# Revit family: LBA_LBATPMR
name_source: partatom
category: Equipement spécialisé
revit_build: Autodesk Revit 2017 (Build: 20160225_1515(x64)
units: mm (PartAtom-declared; Revit-internal decimal feet)

## family parameters
Basée sur le plan de construction = Non
Cote de connecteur circulaire = Utiliser le diamètre
Couper avec des vides une fois chargée = Non
Partagée = Non
Point de calcul de pièce = Non
Toujours verticalement = Oui
Type d'élément = Normal

## types (1)
- Portillon PMR
    Fabricant = La Barrière Automatique
    Matériau_barreaux = ALU_INOX
    Matériau_base = BLANC_MAT
    Modèle = PMR
    URL = https://barriere-automatique.com
    courbe_barreaux_centre = 325 mm  [stored 1.06627 ft]
    d_poteau_centre = 75 mm
    d_poteau_fixes_laterales = 45 mm  [stored 0.147638 ft]
    demi_d_laterale = 23 mm
    diamètre_barreaux = 33 mm  [stored 0.108268 ft]
    diamètre_poteau_tournant = 60 mm  [stored 0.19685 ft]
    diamètre_poteaux = 75 mm
    dimension_plaques = 100 mm  [stored 0.328084 ft]
    distance_laterale = 530 mm  [stored 1.73885 ft]
    formule_positon_tourniquet = 768 mm
    h_b = 20 mm  [stored 0.0656168 ft]
    h_poste = 2110 mm  [stored 6.92257 ft]
    hauteur_controle_accèss = 810 mm  [stored 2.65748 ft]
    hauteur_passage = 2000 mm  [stored 6.56168 ft]
    hauteur_volume_emprise = 2383 mm  [stored 7.81824 ft]
    largeur_barreaux_centre = 360 mm  [stored 1.1811 ft]
    largeur_controle_accèss = 200 mm  [stored 0.656168 ft]
    largeur_passage = 685 mm  [stored 2.24738 ft]
    largeur_toiture = 3200 mm  [stored 10.4987 ft]
    largeur_volume_emprise = 3370 mm  [stored 11.0564 ft]
    longueur_assemblages_laterales = 1380 mm  [stored 4.52756 ft]
    longueur_barreaux_centre = 1300 mm  [stored 4.26509 ft]
    longueur_barreaux_tournants = 685 mm  [stored 2.24738 ft]
    longueur_controle_accèss = 100 mm  [stored 0.328084 ft]
    longueur_toiture = 1464 mm
    longueur_volume_emprise = 1782 mm
    position_barreaux_turnants = 510 mm  [stored 1.67323 ft]
    position_portillon = 535 mm  [stored 1.75525 ft]
    poteau_portillon_lateral = 1545 mm

note: [stored X ft] marks values corroborated as IEEE doubles in the binary element streams (Revit-internal decimal feet)
